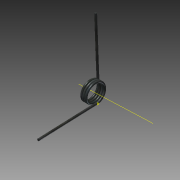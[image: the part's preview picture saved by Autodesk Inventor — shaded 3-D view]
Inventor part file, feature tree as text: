
AUTODESK INVENTOR PART (.ipt)
format: ipt  version: 2014 (Build 180170000, 170)  size: 224,256 bytes
history: native  units: in
note: dims shown in document units (in); Inventor stores cm internally (conversion verified against a paired STEP export)
features: other x4, plane x1, sketch x1, imported_body x1
ambient origin geometry x8: Origin, YZ Plane, XZ Plane, XY Plane, X Axis, Y Axis, Z Axis, Center Point
bodies: Body1 (feature_tree)
feature tree (7):
  parser-record x1  (decoder bookkeeping rows leaked as tree rows — omitted from the tree; the rows remain in map.json)
  other  "9271K1301"
  other  "Work Point1"
  plane  "Work Plane1"
  sketch  "Sketch1"
  other  "Work Axis1"
  imported_body  "Base1"
